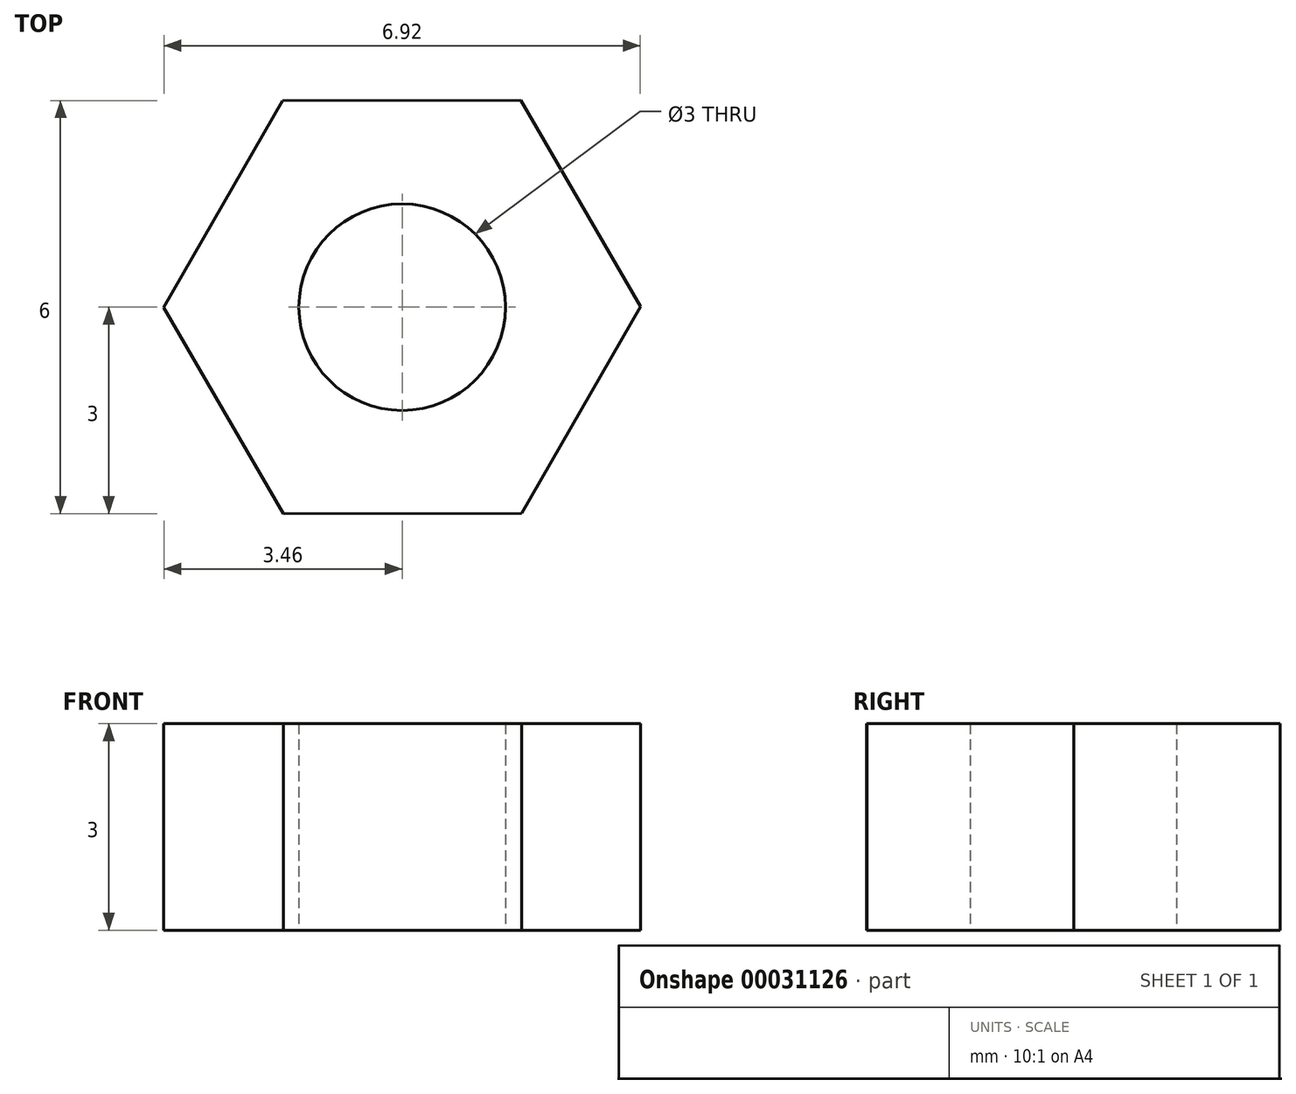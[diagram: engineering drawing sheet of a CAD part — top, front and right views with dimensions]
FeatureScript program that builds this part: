
annotation { "Feature Type Name" : "Feature", "Feature Type Description" : "" }
export const myFeature = defineFeature(function(context is Context, id is Id, definition is map)
    precondition{}
    {
        {
            var Q0;
            Q0=qCreatedBy(makeId("Top.planeOp"),FACE);
            var sketch = newSketch(context, id + "F0", { "sketchPlane" : qUnion([Q0])});
            skCircle(sketch, "E0.cCircle", {"center": v(0, 0) * mm, "radius": 3 * mm, "construction": true});
            skLineSegment(sketch, "E0.0", {"start": v(1.73, 3) * mm, "end": v(3.46, 0) * mm});
            skLineSegment(sketch, "E0.1", {"start": v(3.46, 0) * mm, "end": v(1.74, -3) * mm});
            skLineSegment(sketch, "E0.2", {"start": v(1.74, -3) * mm, "end": v(-1.73, -3) * mm});
            skLineSegment(sketch, "E0.3", {"start": v(-1.73, -3) * mm, "end": v(-3.46, 0) * mm});
            skLineSegment(sketch, "E0.4", {"start": v(-3.46, 0) * mm, "end": v(-1.74, 3) * mm});
            skLineSegment(sketch, "E0.5", {"start": v(-1.74, 3) * mm, "end": v(1.73, 3) * mm});
            skPoint(sketch, "E0.0.midPoint", {"position": v(2.6, 1.5) * mm});
            skCircle(sketch, "E1", {"center": v(0, 0) * mm, "radius": 1.5 * mm});
            skSolve(sketch);
        }
        {
            var Q0;
            Q0=makeQuery(id+"F0.imprint","IMPRINT",FACE,{"disambiguationData":[TD([[makeQuery(id+"F0.imprint","IMPRINT",EDGE,{"derivedFrom":sQuery(id+"F0.wireOp",EDGE,"E0.0")}),-1.0]])]});
            extrude(context, id + "F1", {"entities" : qUnion([Q0]), "depth" : 3 * mm});
        }
    });
